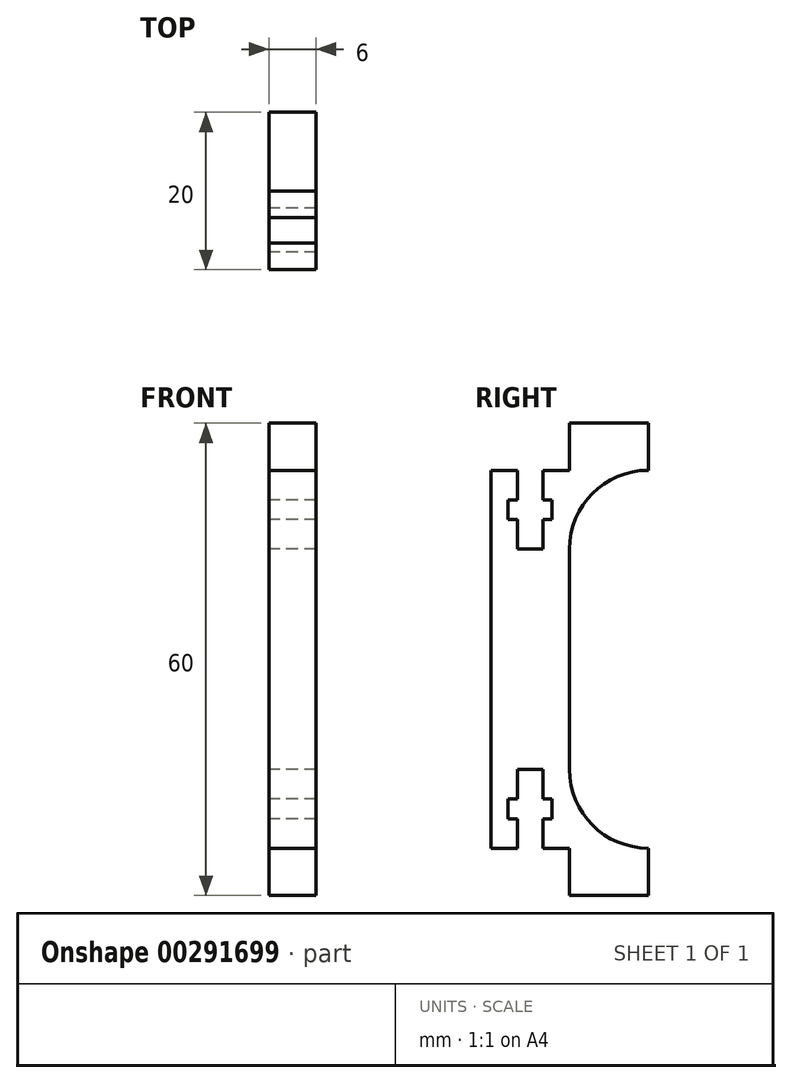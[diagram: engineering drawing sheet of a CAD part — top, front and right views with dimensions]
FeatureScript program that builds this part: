
annotation { "Feature Type Name" : "Feature", "Feature Type Description" : "" }
export const myFeature = defineFeature(function(context is Context, id is Id, definition is map)
    precondition{}
    {
        {
            var Q0;
            Q0=qCreatedBy(makeId("Right.planeOp"),FACE);
            var sketch = newSketch(context, id + "F0", { "sketchPlane" : qUnion([Q0])});
            skLineSegment(sketch, "E0", {"start": v(0, 48) * mm, "end": v(0, 0) * mm});
            skLineSegment(sketch, "E1", {"start": v(10, 0) * mm, "end": v(10, -6) * mm});
            skLineSegment(sketch, "E2", {"start": v(10, -6) * mm, "end": v(20, -6) * mm});
            skLineSegment(sketch, "E3", {"start": v(20, -6) * mm, "end": v(20, 0) * mm});
            skArc(sketch, "E4", {"start": v(10, 10) * mm, "mid": v(12.93, 2.93) * mm, "end": v(20, 0) * mm});
            skLineSegment(sketch, "E5", {"start": v(20, 0) * mm, "end": v(20, 48) * mm, "construction": true});
            skLineSegment(sketch, "E6", {"start": v(10, 10) * mm, "end": v(10, 38) * mm});
            skArc(sketch, "E7", {"start": v(20, 48) * mm, "mid": v(12.93, 45.07) * mm, "end": v(10, 38) * mm});
            skLineSegment(sketch, "E8", {"start": v(10, 10) * mm, "end": v(20, 10) * mm, "construction": true});
            skLineSegment(sketch, "E9", {"start": v(10, 38) * mm, "end": v(20, 38) * mm, "construction": true});
            skLineSegment(sketch, "E10", {"start": v(20, 48) * mm, "end": v(20, 54) * mm});
            skLineSegment(sketch, "E11", {"start": v(20, 54) * mm, "end": v(10, 54) * mm});
            skLineSegment(sketch, "E12", {"start": v(10, 54) * mm, "end": v(10, 48) * mm});
            skLineSegment(sketch, "E13", {"start": v(0, 0) * mm, "end": v(3.4, 0) * mm});
            skLineSegment(sketch, "E14", {"start": v(3.4, 0) * mm, "end": v(3.4, 3.75) * mm});
            skLineSegment(sketch, "E15", {"start": v(3.4, 3.75) * mm, "end": v(2.2, 3.75) * mm});
            skLineSegment(sketch, "E16", {"start": v(2.2, 3.75) * mm, "end": v(2.2, 6.25) * mm});
            skLineSegment(sketch, "E17", {"start": v(2.2, 6.25) * mm, "end": v(3.4, 6.25) * mm});
            skLineSegment(sketch, "E18", {"start": v(3.4, 6.25) * mm, "end": v(3.4, 10) * mm});
            skLineSegment(sketch, "E19", {"start": v(3.4, 10) * mm, "end": v(5, 10) * mm});
            skLineSegment(sketch, "E20", {"start": v(5, 10) * mm, "end": v(5, 0) * mm, "construction": true});
            skLineSegment(sketch, "E21.MirrorCS", {"start": v(6.6, 10) * mm, "end": v(5, 10) * mm});
            skLineSegment(sketch, "E22.MirrorCS", {"start": v(6.6, 6.25) * mm, "end": v(6.6, 10) * mm});
            skLineSegment(sketch, "E23.MirrorCS", {"start": v(7.8, 6.25) * mm, "end": v(6.6, 6.25) * mm});
            skLineSegment(sketch, "E24.MirrorCS", {"start": v(7.8, 3.75) * mm, "end": v(7.8, 6.25) * mm});
            skLineSegment(sketch, "E25.MirrorCS", {"start": v(6.6, 3.75) * mm, "end": v(7.8, 3.75) * mm});
            skLineSegment(sketch, "E26.MirrorCS", {"start": v(10, 0) * mm, "end": v(6.6, 0) * mm});
            skLineSegment(sketch, "E27.MirrorCS", {"start": v(6.6, 0) * mm, "end": v(6.6, 3.75) * mm});
            skLineSegment(sketch, "E28", {"start": v(0, 24) * mm, "end": v(20, 24) * mm, "construction": true});
            skLineSegment(sketch, "E29.MirrorCS", {"start": v(6.6, 38) * mm, "end": v(5, 38) * mm});
            skLineSegment(sketch, "E30.MirrorCS", {"start": v(2.2, 41.75) * mm, "end": v(3.4, 41.75) * mm});
            skLineSegment(sketch, "E31.MirrorCS", {"start": v(7.8, 44.25) * mm, "end": v(7.8, 41.75) * mm});
            skLineSegment(sketch, "E32.MirrorCS", {"start": v(3.4, 44.25) * mm, "end": v(2.2, 44.25) * mm});
            skLineSegment(sketch, "E33.MirrorCS", {"start": v(3.4, 38) * mm, "end": v(5, 38) * mm});
            skLineSegment(sketch, "E34.MirrorCS", {"start": v(6.6, 41.75) * mm, "end": v(6.6, 38) * mm});
            skLineSegment(sketch, "E35.MirrorCS", {"start": v(3.4, 41.75) * mm, "end": v(3.4, 38) * mm});
            skLineSegment(sketch, "E36.MirrorCS", {"start": v(7.8, 41.75) * mm, "end": v(6.6, 41.75) * mm});
            skLineSegment(sketch, "E37.MirrorCS", {"start": v(6.6, 44.25) * mm, "end": v(7.8, 44.25) * mm});
            skLineSegment(sketch, "E38.MirrorCS", {"start": v(2.2, 44.25) * mm, "end": v(2.2, 41.75) * mm});
            skLineSegment(sketch, "E39.MirrorCS", {"start": v(3.4, 48) * mm, "end": v(3.4, 44.25) * mm});
            skLineSegment(sketch, "E40.MirrorCS", {"start": v(0, 48) * mm, "end": v(3.4, 48) * mm});
            skLineSegment(sketch, "E41.MirrorCS", {"start": v(10, 48) * mm, "end": v(6.6, 48) * mm});
            skLineSegment(sketch, "E42.MirrorCS", {"start": v(6.6, 48) * mm, "end": v(6.6, 44.25) * mm});
            skPoint(sketch, "E43.endSnap0", {"position": v(7.8, 5) * mm});
            skSolve(sketch);
        }
        {
            var Q0;
            Q0=qSketchRegion(id+"F0",true);
            extrude(context, id + "F1", {"entities" : qUnion([Q0]), "depth" : 6 * mm});
        }
    });
